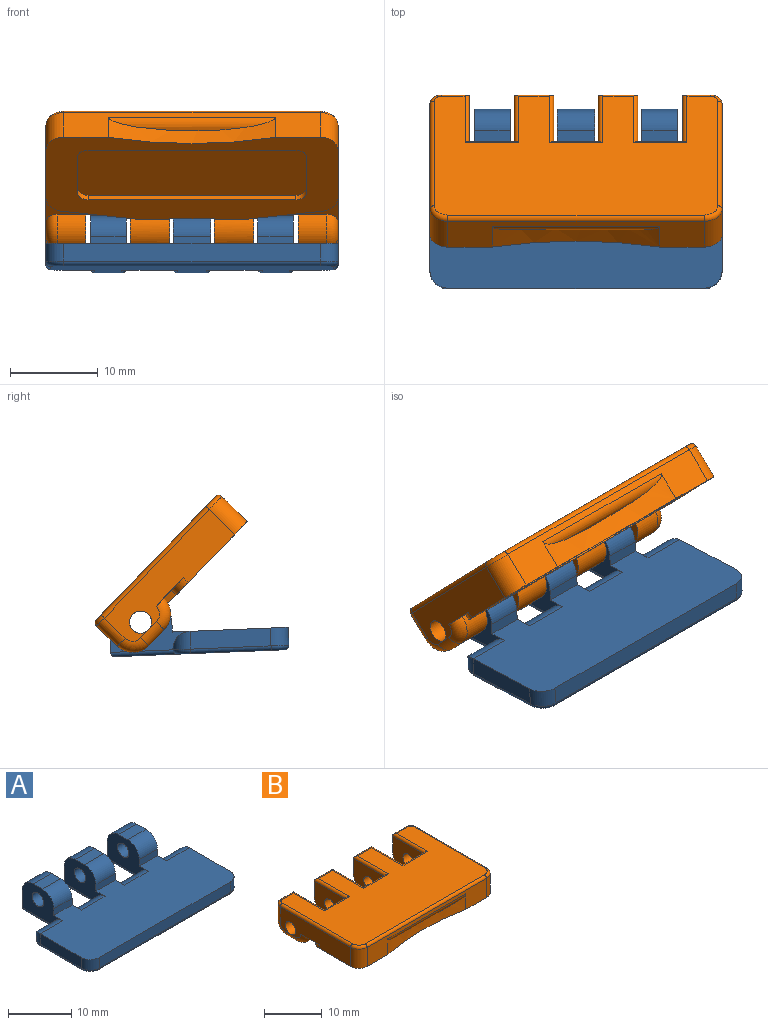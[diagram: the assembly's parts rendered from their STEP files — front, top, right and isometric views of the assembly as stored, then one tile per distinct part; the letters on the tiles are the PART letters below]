
ASSEMBLY  parts=2 mates=1
PART A: 57 faces, bbox 33.6x20.5x6.4 mm
  f0: plane 32.26x19.3mm, normal (0,0,-1), area 458.1mm2, adj f31,f32,f33,f34,f35,f36,f37,f38
  f1: plane 4.06x1.27mm, normal (0,-1,0), area 5.2mm2, adj f13,f15,f19,f20
  f2: plane 4.06x1.27mm, normal (0,-1,0), area 5.2mm2, adj f13,f14,f18,f24
  f3: plane 4.32x1.27mm, normal (0,-1,0), area 5.5mm2, adj f13,f16,f17,f21
  f4: plane 4.06x2.03mm, normal (0,0,1), area 8.3mm2, adj f15,f19,f20,f22
  f5: plane 4.06x2.03mm, normal (0,0,1), area 8.3mm2, adj f14,f18,f24,f25
  f6: plane 4.32x2.03mm, normal (0,0,1), area 8.8mm2, adj f16,f17,f21,f23
  f7: plane 4.06x3.3mm, normal (0,1,0), area 13.4mm2, adj f15,f19,f22,f41
  f8: plane 4.06x3.3mm, normal (0,1,0), area 13.4mm2, adj f14,f18,f25,f36
  f9: plane 4.32x3.3mm, normal (0,1,0), area 14.3mm2, adj f16,f17,f23,f33
  f10: plane 9.14x2.03mm, normal (-1,0,0), area 18.6mm2, adj f13,f29,f47,f50
  f11: plane 29.21x2.03mm, normal (0,-1,0), area 59.4mm2, adj f13,f29,f30,f46
  f12: plane 9.14x2.03mm, normal (1,0,0), area 18.6mm2, adj f13,f30,f42,f53
  f13: plane 33.27x13.21mm, normal (0,0,1), area 395.4mm2, adj f1,f2,f3,f10,f11,f12,f14,f15
  f14: plane 9.14x5.84mm, normal (1,0,0), area 34.6mm2, adj f2,f5,f8,f13,f24,f25,f27,f38
  f15: plane 9.14x5.84mm, normal (1,0,0), area 34.6mm2, adj f1,f4,f7,f13,f20,f22,f26,f39
  f16: plane 9.14x5.84mm, normal (-1,0,0), area 34.6mm2, adj f3,f6,f9,f13,f21,f23,f28,f35
  f17: plane 9.14x5.84mm, normal (1,0,0), area 34.6mm2, adj f3,f6,f9,f13,f21,f23,f28,f31
  f18: plane 9.14x5.84mm, normal (-1,0,0), area 34.6mm2, adj f2,f5,f8,f13,f24,f25,f27,f34
  f19: plane 9.14x5.84mm, normal (-1,0,0), area 34.6mm2, adj f1,f4,f7,f13,f20,f22,f26,f43
  f20: cylinder r=2.54mm len=4.06mm, axis (1,0,0), area 16.2mm2, adj f1,f4,f15,f19
  f21: cylinder r=2.54mm len=4.32mm, axis (1,0,0), area 17.2mm2, adj f3,f6,f16,f17
  f22: cylinder r=2.54mm len=4.06mm, axis (-1,0,0), area 16.2mm2, adj f4,f7,f15,f19
  f23: cylinder r=2.54mm len=4.32mm, axis (-1,0,0), area 17.2mm2, adj f6,f9,f16,f17
  f24: cylinder r=2.54mm len=4.06mm, axis (1,0,0), area 16.2mm2, adj f2,f5,f14,f18
  f25: cylinder r=2.54mm len=4.06mm, axis (-1,0,0), area 16.2mm2, adj f5,f8,f14,f18
  f26: cylinder r=1.27mm len=4.06mm, axis (1,0,0), area 32.4mm2, adj f15,f19
  f27: cylinder r=1.27mm len=4.06mm, axis (1,0,0), area 32.4mm2, adj f14,f18
  f28: cylinder r=1.27mm len=4.32mm, axis (1,0,0), area 34.5mm2, adj f16,f17
  f29: cylinder r=2.03mm len=2.03mm, axis (0,0,1), area 6.5mm2, adj f10,f11,f13,f48
  f30: cylinder r=2.03mm len=2.03mm, axis (0,0,-1), area 6.5mm2, adj f11,f12,f13,f44
  f31: cylinder r=0.51mm len=7.62mm, axis (0,-1,0), area 5.7mm2, adj f0,f17,f32,f33
  f32: cylinder r=0.51mm len=6.35mm, axis (1,0,0), area 4.6mm2, adj f0,f31,f34,f55
  f33: cylinder r=0.51mm len=4.32mm, axis (-1,0,0), area 3.2mm2, adj f0,f9,f31,f35
  f34: cylinder r=0.51mm len=7.62mm, axis (0,1,0), area 5.7mm2, adj f0,f18,f32,f36
  f35: cylinder r=0.51mm len=7.62mm, axis (0,1,0), area 5.7mm2, adj f0,f16,f33,f37
  f36: cylinder r=0.51mm len=4.06mm, axis (-1,0,0), area 2.9mm2, adj f0,f8,f34,f38
  f37: cylinder r=0.51mm len=6.35mm, axis (1,0,0), area 4.6mm2, adj f0,f35,f39,f56
  f38: cylinder r=0.51mm len=7.62mm, axis (0,-1,0), area 5.7mm2, adj f0,f14,f36,f40
  f39: cylinder r=0.51mm len=7.62mm, axis (0,-1,0), area 5.7mm2, adj f0,f15,f37,f41
  f40: cylinder r=0.51mm len=3.56mm, axis (1,0,0), area 2.6mm2, adj f0,f38,f52,f54
  f41: cylinder r=0.51mm len=4.06mm, axis (-1,0,0), area 2.9mm2, adj f0,f7,f39,f43
  f42: cylinder r=0.51mm len=9.14mm, axis (0,1,0), area 7.3mm2, adj f0,f12,f44,f54
  f43: cylinder r=0.51mm len=7.62mm, axis (0,1,0), area 5.7mm2, adj f0,f19,f41,f45
  f44: torus R=1.52mm, axis (0,0,1), area 2.3mm2, adj f0,f30,f42,f46
  f45: cylinder r=0.51mm len=3.56mm, axis (1,0,0), area 2.6mm2, adj f0,f43,f49,f51
  f46: cylinder r=0.51mm len=29.21mm, axis (1,0,0), area 23.3mm2, adj f0,f11,f44,f48
  f47: cylinder r=0.51mm len=9.14mm, axis (0,-1,0), area 7.3mm2, adj f0,f10,f48,f51
  f48: torus R=1.52mm, axis (0,0,1), area 2.3mm2, adj f0,f29,f46,f47
  f49: cylinder r=2.03mm len=5.08mm, axis (1,0,0), area 13.9mm2, adj f13,f19,f45,f50
  f50: cylinder r=2.03mm len=2.03mm, axis (0,0,1), area 4.1mm2, adj f10,f49,f51
  f51: torus R=1.52mm, axis (0,0,1), area 2.3mm2, adj f0,f45,f47,f50
  f52: cylinder r=2.03mm len=5.08mm, axis (1,0,0), area 13.9mm2, adj f13,f14,f40,f53
  f53: cylinder r=2.03mm len=2.03mm, axis (0,0,-1), area 4.1mm2, adj f12,f52,f54
  f54: torus R=1.52mm, axis (0,0,1), area 2.3mm2, adj f0,f40,f42,f53
  f55: cylinder r=2.03mm len=5.33mm, axis (1,0,0), area 17mm2, adj f13,f17,f18,f32
  f56: cylinder r=2.03mm len=5.33mm, axis (1,0,0), area 17mm2, adj f13,f15,f16,f37
PART B: 81 faces, bbox 33.6x20.9x6.6 mm
  f0: plane 29.21x4.06mm, normal (0,-1,0), area 55.8mm2, adj f1,f44,f45,f47,f48,f74
  f1: plane 33.27x13.01mm, normal (0,0,-1), area 195.3mm2, adj f0,f8,f9,f10,f11,f12,f13,f14
  f2: plane 4.51x2.54mm, normal (0,0,-1), area 11.5mm2, adj f26,f30,f33,f36
  f3: plane 4.51x2.54mm, normal (0,0,-1), area 11.5mm2, adj f23,f27,f32,f35
  f4: plane 3.24x2.54mm, normal (0,0,-1), area 8.2mm2, adj f24,f31,f34,f55
  f5: plane 3.3x3.24mm, normal (0,1,0), area 10.7mm2, adj f29,f38,f57,f66
  f6: plane 4.51x3.3mm, normal (0,1,0), area 14.9mm2, adj f26,f30,f33,f63
  f7: plane 4.51x3.3mm, normal (0,1,0), area 14.9mm2, adj f23,f27,f32,f71
  f8: plane 8.92x1.32mm, normal (-0.15,0.99,0), area 6.5mm2, adj f1,f18,f36,f43
  f9: plane 17.21x4.57mm, normal (-1,0,0), area 63.3mm2, adj f1,f18,f40,f43,f44,f57,f58,f59
  f10: plane 17.21x4.57mm, normal (1,0,0), area 63.3mm2, adj f1,f17,f42,f45,f46,f53,f54,f55
  f11: plane 5.33x0.76mm, normal (1,0,0), area 4.1mm2, adj f1,f19,f49,f51
  f12: plane 23.62x0.76mm, normal (0,-1,0), area 18mm2, adj f1,f19,f49,f50
  f13: plane 5.33x0.76mm, normal (-1,0,0), area 4.1mm2, adj f1,f19,f50,f52
  f14: plane 23.62x0.76mm, normal (0,1,0), area 18mm2, adj f1,f19,f51,f52
  f15: plane 8.92x1.32mm, normal (0.15,0.99,0), area 6.5mm2, adj f1,f17,f35,f46
  f16: plane 32.26x19.49mm, normal (0,0,1), area 488.2mm2, adj f61,f62,f63,f64,f65,f66,f67,f68
  f17: plane 9.86x4.48mm, normal (0,0,-1), area 8.2mm2, adj f10,f15,f22,f34,f35,f46,f56
  f18: plane 9.86x4.48mm, normal (0,0,-1), area 8.2mm2, adj f8,f9,f28,f36,f37,f43,f60
  f19: plane 26.16x7.87mm, normal (0,0,-1), area 204.6mm2, adj f11,f12,f13,f14,f49,f50,f51,f52
  f20: plane 3.24x2.54mm, normal (0,0,-1), area 8.2mm2, adj f29,f37,f38,f59
  f21: plane 3.3x3.24mm, normal (0,1,0), area 10.7mm2, adj f24,f31,f53,f79
  f22: plane 5.08x3.3mm, normal (0,1,0), area 16.8mm2, adj f17,f23,f24,f75
  f23: plane 7.62x5.84mm, normal (1,0,0), area 36.7mm2, adj f3,f7,f22,f32,f35,f41,f73
  f24: plane 7.62x5.84mm, normal (-1,0,0), area 36.7mm2, adj f4,f21,f22,f31,f34,f42,f77
  f25: plane 5.08x4.06mm, normal (0,1,0), area 20.6mm2, adj f1,f26,f27,f67
  f26: plane 7.62x5.84mm, normal (1,0,0), area 36.7mm2, adj f1,f2,f6,f25,f33,f36,f39,f65
  f27: plane 7.62x5.84mm, normal (-1,0,0), area 36.7mm2, adj f1,f3,f7,f25,f32,f35,f41,f69
  f28: plane 5.08x3.3mm, normal (0,1,0), area 16.8mm2, adj f18,f29,f30,f62
  f29: plane 7.62x5.84mm, normal (1,0,0), area 36.7mm2, adj f5,f20,f28,f37,f38,f40,f64
  f30: plane 7.62x5.84mm, normal (-1,0,0), area 36.7mm2, adj f2,f6,f28,f33,f36,f39,f61
  f31: cylinder r=2.54mm len=3.24mm, axis (1,0,0), area 12.9mm2, adj f4,f21,f24,f54
  f32: cylinder r=2.54mm len=4.51mm, axis (1,0,0), area 18mm2, adj f3,f7,f23,f27
  f33: cylinder r=2.54mm len=4.51mm, axis (1,0,0), area 18mm2, adj f2,f6,f26,f30
  f34: cylinder r=2.54mm len=3.24mm, axis (-1,0,0), area 12.9mm2, adj f4,f17,f24,f56
  f35: cylinder r=2.54mm len=4.51mm, axis (-1,0,0), area 14.9mm2, adj f1,f3,f15,f17,f23,f27
  f36: cylinder r=2.54mm len=4.51mm, axis (-1,0,0), area 14.9mm2, adj f1,f2,f8,f18,f26,f30
  f37: cylinder r=2.54mm len=3.24mm, axis (-1,0,0), area 12.9mm2, adj f18,f20,f29,f60
  f38: cylinder r=2.54mm len=3.24mm, axis (1,0,0), area 12.9mm2, adj f5,f20,f29,f58
  f39: cylinder r=1.27mm len=4.51mm, axis (-1,0,0), area 36mm2, adj f26,f30
  f40: cylinder r=1.27mm len=4.51mm, axis (-1,0,0), area 36mm2, adj f9,f29
  f41: cylinder r=1.27mm len=4.51mm, axis (-1,0,0), area 36mm2, adj f23,f27
  f42: cylinder r=1.27mm len=4.51mm, axis (-1,0,0), area 36mm2, adj f10,f24
  f43: cylinder r=2.03mm len=2.01mm, axis (0,0,-1), area 2.2mm2, adj f1,f8,f9,f18
  f44: cylinder r=2.03mm len=4.06mm, axis (0,0,-1), area 13mm2, adj f0,f1,f9,f72
  f45: cylinder r=2.03mm len=4.06mm, axis (0,0,1), area 13mm2, adj f0,f1,f10,f76
  f46: cylinder r=2.03mm len=2.01mm, axis (0,0,1), area 2.2mm2, adj f1,f10,f15,f17
  f47: cylinder r=46.81mm len=19.05mm, axis (0,0,-1), area 43.4mm2, adj f0,f1,f48
  f48: cylinder r=1.27mm len=19.05mm, axis (1,0,0), area 25mm2, adj f0,f47
  f49: cylinder r=1.27mm len=1.27mm, axis (0,0,-1), area 1.5mm2, adj f1,f11,f12,f19
  f50: cylinder r=1.27mm len=1.27mm, axis (0,0,1), area 1.5mm2, adj f1,f12,f13,f19
  f51: cylinder r=1.27mm len=1.27mm, axis (0,0,1), area 1.5mm2, adj f1,f11,f14,f19
  f52: cylinder r=1.27mm len=1.27mm, axis (0,0,-1), area 1.5mm2, adj f1,f13,f14,f19
  f53: cylinder r=1.27mm len=3.3mm, axis (0,0,-1), area 6.6mm2, adj f10,f21,f54,f80
  f54: torus R=1.27mm, axis (1,0,0), area 6.5mm2, adj f10,f31,f53,f55
  f55: cylinder r=1.27mm len=2.54mm, axis (0,-1,0), area 5.1mm2, adj f4,f10,f54,f56
  f56: torus R=1.27mm, axis (1,0,0), area 6.5mm2, adj f10,f17,f34,f55
  f57: cylinder r=1.27mm len=3.3mm, axis (0,0,1), area 6.6mm2, adj f5,f9,f58,f68
  f58: torus R=1.27mm, axis (1,0,0), area 6.5mm2, adj f9,f38,f57,f59
  f59: cylinder r=1.27mm len=2.54mm, axis (0,1,0), area 5.1mm2, adj f9,f20,f58,f60
  f60: torus R=1.27mm, axis (1,0,0), area 6.5mm2, adj f9,f18,f37,f59
  f61: cylinder r=0.51mm len=8.13mm, axis (0,-1,0), area 6.1mm2, adj f16,f30,f62,f63
  f62: cylinder r=0.51mm len=6.1mm, axis (-1,0,0), area 4.3mm2, adj f16,f28,f61,f64
  f63: cylinder r=0.51mm len=4.51mm, axis (-1,0,0), area 3.3mm2, adj f6,f16,f61,f65
  f64: cylinder r=0.51mm len=8.13mm, axis (0,1,0), area 6.1mm2, adj f16,f29,f62,f66
  f65: cylinder r=0.51mm len=8.13mm, axis (0,1,0), area 6.1mm2, adj f16,f26,f63,f67
  f66: cylinder r=0.51mm len=3.24mm, axis (-1,0,0), area 2.4mm2, adj f5,f16,f64,f68
  f67: cylinder r=0.51mm len=6.1mm, axis (-1,0,0), area 4.3mm2, adj f16,f25,f65,f69
  f68: torus R=0.76mm, axis (0,0,1), area 1.4mm2, adj f16,f57,f66,f70
  f69: cylinder r=0.51mm len=8.13mm, axis (0,-1,0), area 6.1mm2, adj f16,f27,f67,f71
  f70: cylinder r=0.51mm len=17.21mm, axis (0,1,0), area 13.7mm2, adj f9,f16,f68,f72
  f71: cylinder r=0.51mm len=4.51mm, axis (-1,0,0), area 3.3mm2, adj f7,f16,f69,f73
  f72: torus R=1.52mm, axis (0,0,1), area 2.3mm2, adj f16,f44,f70,f74
  f73: cylinder r=0.51mm len=8.13mm, axis (0,1,0), area 6.1mm2, adj f16,f23,f71,f75
  f74: cylinder r=0.51mm len=29.21mm, axis (1,0,0), area 23.3mm2, adj f0,f16,f72,f76
  f75: cylinder r=0.51mm len=6.1mm, axis (-1,0,0), area 4.3mm2, adj f16,f22,f73,f77
  f76: torus R=1.52mm, axis (0,0,1), area 2.3mm2, adj f16,f45,f74,f78
  f77: cylinder r=0.51mm len=8.13mm, axis (0,-1,0), area 6.1mm2, adj f16,f24,f75,f79
  f78: cylinder r=0.51mm len=17.21mm, axis (0,-1,0), area 13.7mm2, adj f10,f16,f76,f80
  f79: cylinder r=0.51mm len=3.24mm, axis (-1,0,0), area 2.4mm2, adj f16,f21,f77,f80
  f80: torus R=0.76mm, axis (0,0,1), area 1.4mm2, adj f16,f53,f78,f79
PLACE A rot(axis=(-1,0,0),2.3deg) t=(-1.14,-6.91,-9.17)mm
PLACE B rot(axis=(-1,0,0),46deg) t=(2.42,-0.78,3.94)mm
MATE revolute A.f26 <-> B.f39  axis (-1,0,0) through (3.37,9.99,-6.05)mm
